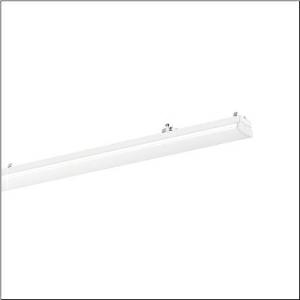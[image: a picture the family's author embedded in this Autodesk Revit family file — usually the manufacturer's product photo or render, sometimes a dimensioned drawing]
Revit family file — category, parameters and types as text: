
# Revit family: licross_11_recessed_opal_mo_51tl1ddn425g
name_source: partatom
category: Lighting Fixtures
units: mm (PartAtom-declared; Revit-internal decimal feet)

## family parameters
Cut with Voids When Loaded = No
Host = Face
Light Source = No
Part Type = Normal
Room Calculation Point = No
Round Connector Dimension = Use Diameter
Shared = No

## types (1)
- --- (1 x LED, 2750 lm, 15.7 W, 4000K)
    Apparent Load = 16 VA
    CIE Flux Codes = 44 73 91 87 100
    Color Rendering = 80
    Color Temperature = 4000K
    Default Elevation = 1800 mm
    Description = Licross 11 recessed opal MO, luminaire insert, of sheet steel, coil coated, white, length: 1.500mm, width: 76mm, height: 87mm, LED rated luminous flux: 2.750lm, light colour: 840, SDCM (Standard Deviation of Colour Matching)MacAdam ≤ 2 SDCM (initial), control gear: DALI 2, with plug, 5-pole, with phase selection, mains connection: 220..240V, AC, 50/60Hz, rated input power: 16W, internal wiring halogen-free, primary optical cover: cover, of PMMA, light emission: direct with ceiling illumination distribution, primary light characteristic: symmetric, protection rating (complete): IP40, insulation class (complete): insulation class I (protective earthing), certification: CE, ENEC, VDE, UKCA, protection symbol: D if used in an environment without relevant dust loads with corresponding accessories, impact resistance: IK06, permissible ambient temperature for indoor applications: -25..+50°C, corresponds to IFS (International Featured Standards) requirements for safety and quality in the food industry, reducing of maximum allowable ambient temperature of 5°C with ceiling mounting, LABS conformity tested according to VDMA 24364:2018-05, The light source and the operating device comply with the requirements of the Ecodesign Regulation (EU) 2019/2020 and are replaceable in accordance with this regulation, packaging unit: 1 piece
    Height = 83 mm
    Lamp = 1 x LED
    Lamp Light Flux = 2750 lm
    Lamp Power = 15.7 W
    Lamp count = 1
    Length = 1500 mm
    Luminous efficacy = 175 lm/W
    Manufacturer = Siteco
    ModVariant = No
    Model = 51TL1DDN425G
    Mounting Place = Ceiling
    Mounting Type = Pendant
    Number of Poles = 1
    OnlyDefault = Yes
    Power Factor = 1
    Product Name = Licross 11 recessed opal MO
    Product group = luminaire insert | ceiling pendant
    ProductGroupID = 901
    Protection Class = Protection class I
    Protection Degree = IP 40
    RLX_Detail_Level = 1
    RLX_Emergency_Light_Flux = 0 lm
    RLX_Emergency_Type = 0
    RLX_Emergency_Type_DB = No
    RlxData = <blob elided: 26629 chars, md5=dc69d9bf>
    Socket = socket
    Standby Power = 0 W
    System Light Flux = 2750 lm
    System Power = 16 W
    Type Comments = factory setting: luminous flux: 100 % | dim-lin: 254 | 101 mA
    Type Image = l_1313666.jpg
    URL = http://relux.com
    VarID = @adj_084009
    Voltage = 0 V
    Weight = 0.00 kg
    Width = 76 mm

## geometry (parser evidence)
native form markers: Blend x4, Sweep x12
no freeform markers — native parametric forms only
